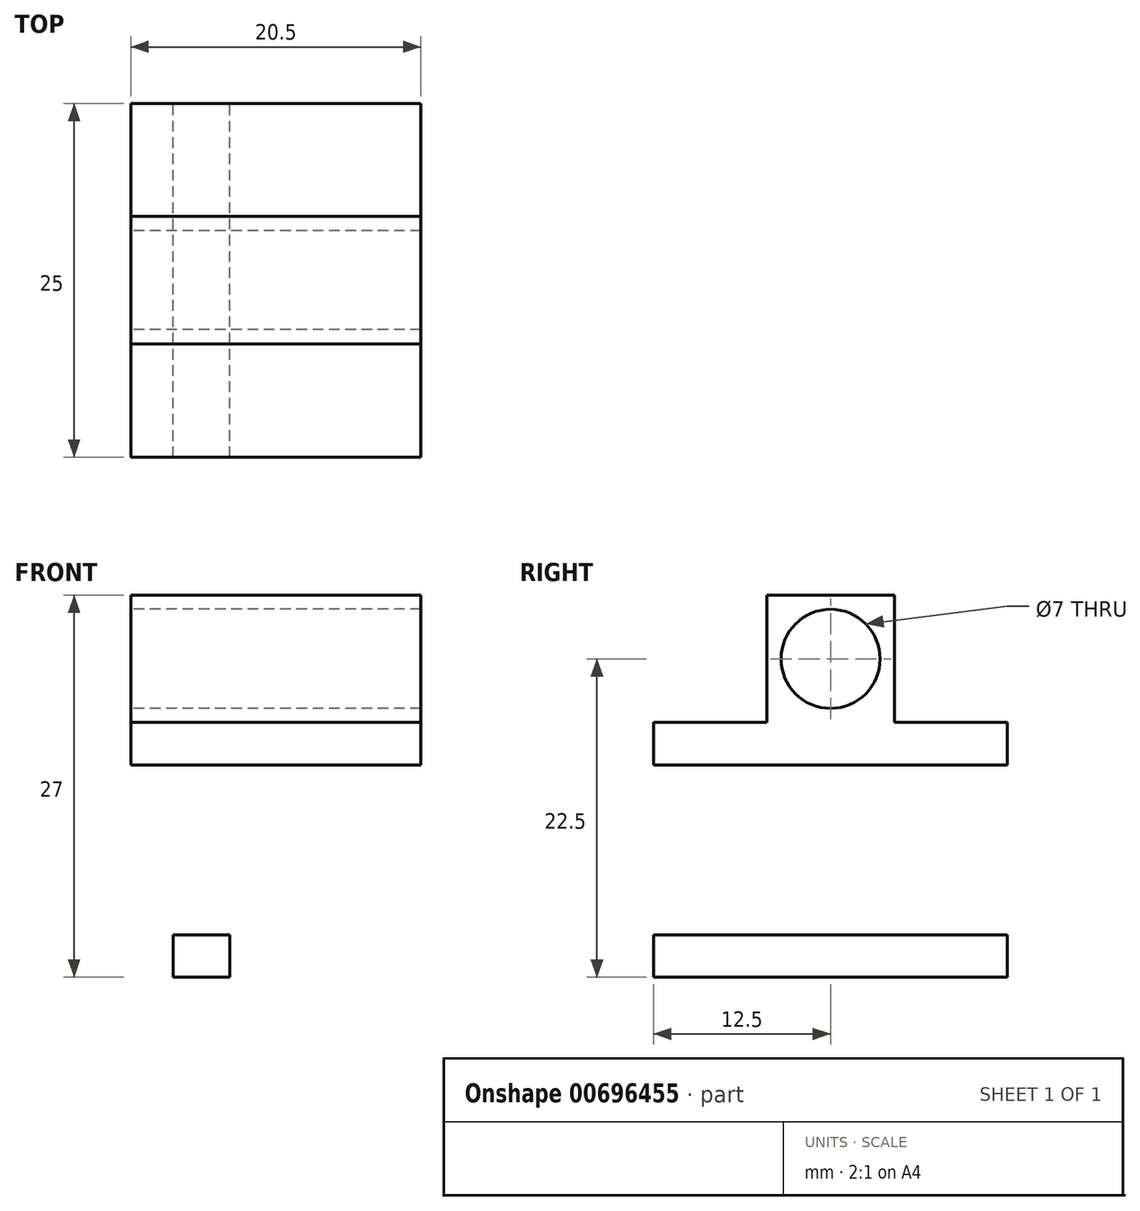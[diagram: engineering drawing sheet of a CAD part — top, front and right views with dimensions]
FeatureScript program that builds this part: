
annotation { "Feature Type Name" : "Feature", "Feature Type Description" : "" }
export const myFeature = defineFeature(function(context is Context, id is Id, definition is map)
    precondition{}
    {
        {
            var Q0;
            Q0=qCreatedBy(makeId("Front.planeOp"),FACE);
            var sketch = newSketch(context, id + "F0", { "sketchPlane" : qUnion([Q0])});
            skLineSegment(sketch, "E0.bottom", {"start": v(-7.9, 0) * mm, "end": v(12.6, 0) * mm});
            skLineSegment(sketch, "E0.top", {"start": v(-7.9, 3) * mm, "end": v(12.6, 3) * mm});
            skLineSegment(sketch, "E0.left", {"start": v(-7.9, 0) * mm, "end": v(-7.9, 3) * mm});
            skLineSegment(sketch, "E0.right", {"start": v(12.6, 0) * mm, "end": v(12.6, 3) * mm});
            skLineSegment(sketch, "E1.bottom", {"start": v(-7.9, 0) * mm, "end": v(-4.9, 0) * mm});
            skLineSegment(sketch, "E1.top", {"start": v(-7.9, -15) * mm, "end": v(-4.9, -15) * mm});
            skLineSegment(sketch, "E1.left", {"start": v(-7.9, 0) * mm, "end": v(-7.9, -15) * mm});
            skLineSegment(sketch, "E1.right", {"start": v(-4.9, 0) * mm, "end": v(-4.9, -15) * mm});
            skLineSegment(sketch, "E2.bottom", {"start": v(12.6, 0) * mm, "end": v(9.6, 0) * mm});
            skLineSegment(sketch, "E2.top", {"start": v(12.6, -15) * mm, "end": v(9.6, -15) * mm});
            skLineSegment(sketch, "E2.left", {"start": v(12.6, 0) * mm, "end": v(12.6, -15) * mm});
            skLineSegment(sketch, "E2.right", {"start": v(9.6, 0) * mm, "end": v(9.6, -15) * mm});
            skLineSegment(sketch, "E3.bottom", {"start": v(-4.9, -15) * mm, "end": v(-0.9, -15) * mm});
            skLineSegment(sketch, "E3.top", {"start": v(-4.9, -12) * mm, "end": v(-0.9, -12) * mm});
            skLineSegment(sketch, "E3.left", {"start": v(-4.9, -15) * mm, "end": v(-4.9, -12) * mm});
            skLineSegment(sketch, "E3.right", {"start": v(-0.9, -15) * mm, "end": v(-0.9, -12) * mm});
            skSolve(sketch);
        }
        {
            var Q0;
            Q0=makeQuery(id+"F0.imprint","IMPRINT",FACE,{"disambiguationData":[TD([[makeQuery(id+"F0.imprint","IMPRINT",EDGE,{"derivedFrom":sQuery(id+"F0.wireOp",EDGE,"E0.bottom")}),1.0]])]});
            var Q1;
            Q1=makeQuery(id+"F0.imprint","IMPRINT",FACE,{"disambiguationData":[TD([[makeQuery(id+"F0.imprint","IMPRINT",EDGE,{"derivedFrom":sQuery(id+"F0.wireOp",EDGE,"E1.bottom")}),-1.0]])]});
            var Q2;
            Q2=makeQuery(id+"F0.imprint","IMPRINT",FACE,{"disambiguationData":[TD([[makeQuery(id+"F0.imprint","IMPRINT",EDGE,{"derivedFrom":sQuery(id+"F0.wireOp",EDGE,"E3.bottom")}),1.0]])]});
            var Q3;
            Q3=makeQuery(id+"F0.imprint","IMPRINT",FACE,{"disambiguationData":[TD([[makeQuery(id+"F0.imprint","IMPRINT",EDGE,{"derivedFrom":sQuery(id+"F0.wireOp",EDGE,"E2.bottom")}),1.0]])]});
            extrude(context, id + "F1", {"entities" : qUnion([Q0, Q1, Q2, Q3]), "depth" : 25 * mm, "offsetDistance" : 25 * mm});
        }
        {
            var Q0;
            Q0=makeQuery(id+"F1.opExtrude","SWEPT_FACE",FACE,{"disambiguationData":[OSD([sQuery(id+"F0.wireOp",EDGE,"E0.top")])]});
            var sketch = newSketch(context, id + "F2", { "sketchPlane" : qUnion([Q0])});
            skLineSegment(sketch, "E4.bottom", {"start": v(-7.9, -8) * mm, "end": v(12.6, -8) * mm});
            skLineSegment(sketch, "E4.top", {"start": v(-7.9, -17) * mm, "end": v(12.6, -17) * mm});
            skLineSegment(sketch, "E4.left", {"start": v(-7.9, -8) * mm, "end": v(-7.9, -17) * mm});
            skLineSegment(sketch, "E4.right", {"start": v(12.6, -8) * mm, "end": v(12.6, -17) * mm});
            skSolve(sketch);
        }
        {
            var Q0;
            Q0=makeQuery(id+"F2.imprint","IMPRINT",FACE,{"disambiguationData":[TD([[makeQuery(id+"F2.imprint","IMPRINT",EDGE,{"derivedFrom":sQuery(id+"F2.wireOp",EDGE,"E4.bottom")}),-1.0]])]});
            extrude(context, id + "F3", {"entities" : qUnion([Q0]), "operationType" : NewBodyOperationType.ADD, "depth" : 9 * mm, "offsetDistance" : 25 * mm});
        }
        {
            var Q0;
            Q0=makeQuery(id+"F3.boolean.opBoolean","MERGE",FACE,{"derivedFrom":[makeQuery(id+"F1.opExtrude","SWEPT_FACE",FACE,{"disambiguationData":[OSD([sQuery(id+"F0.wireOp",EDGE,"E0.left"),sQuery(id+"F0.wireOp",EDGE,"E1.left")])]}),makeQuery(id+"F3.opExtrude","SWEPT_FACE",FACE,{"disambiguationData":[OSD([sQuery(id+"F2.wireOp",EDGE,"E4.left")])]})]});
            var sketch = newSketch(context, id + "F4", { "sketchPlane" : qUnion([Q0])});
            skLineSegment(sketch, "E5", {"start": v(8, 12) * mm, "end": v(17, 3) * mm, "construction": true});
            skLineSegment(sketch, "E6", {"start": v(17, 3) * mm, "end": v(17, 12) * mm, "construction": true});
            skLineSegment(sketch, "E7", {"start": v(17, 12) * mm, "end": v(8, 3) * mm, "construction": true});
            skPoint(sketch, "E8", {"position": v(12.5, 7.5) * mm});
            skCircle(sketch, "E9", {"center": v(12.5, 7.5) * mm, "radius": 3.5 * mm});
            skSolve(sketch);
        }
        {
            var Q0;
            Q0=makeQuery(id+"F4.imprint","IMPRINT",FACE,{"disambiguationData":[TD([[makeQuery(id+"F4.imprint","IMPRINT",EDGE,{"derivedFrom":sQuery(id+"F4.wireOp",EDGE,"E9")}),1.0]])]});
            extrude(context, id + "F5", {"entities" : qUnion([Q0]), "operationType" : NewBodyOperationType.REMOVE, "oppositeDirection" : true, "depth" : 20.5 * mm, "offsetDistance" : 25 * mm});
        }
    });
